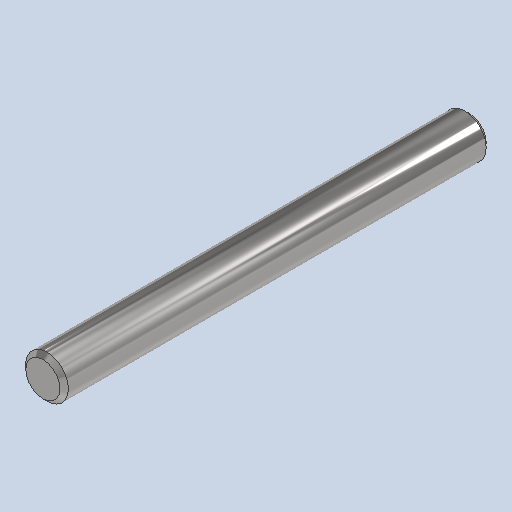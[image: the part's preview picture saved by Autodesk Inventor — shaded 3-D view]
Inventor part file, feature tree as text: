
AUTODESK INVENTOR PART (.ipt)
format: ipt  version: 2022 (Build 260153000, 153)  size: 116,224 bytes
history: native  units: in
note: dims shown in document units (in); Inventor stores cm internally (conversion verified against a paired STEP export)
features: extrude x1, chamfer x1, sketch x1
ambient origin geometry x8: Origin, YZ Plane, XZ Plane, XY Plane, X Axis, Y Axis, Z Axis, Center Point
bodies: Solid1 (feature_tree)
feature tree (3):
  extrude  "Extrusion1"  Depth=1.9685in TaperAngle=0.0deg
  chamfer  "Chamfer1"  Distance=0.0197in Angle=45.0deg
  sketch  "Sketch1"  dims[d0=0.1969in d1=1.9685in d2=0.0in d3=0.0197in d4=0.125in d5=45.0deg]
